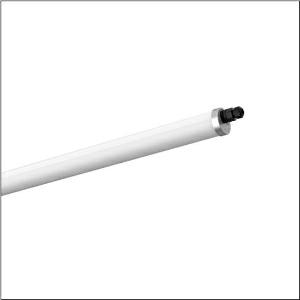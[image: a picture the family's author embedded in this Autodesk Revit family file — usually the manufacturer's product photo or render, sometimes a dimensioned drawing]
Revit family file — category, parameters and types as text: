
# Revit family: monsun_r__31_tube_51ft10dn460a_a449
name_source: partatom
category: Lighting Fixtures
units: mm (PartAtom-declared; Revit-internal decimal feet)

## family parameters
Cut with Voids When Loaded = No
Host = Face
Light Source = No
Part Type = Normal
Room Calculation Point = No
Round Connector Dimension = Use Diameter
Shared = No

## types (1)
- Monsun® 31 Tube (1 x LED, 6500 lm, 40 W, 4000K)
    Apparent Load = 40 VA
    CIE Flux Codes = 42 71 90 91 100
    Color Rendering = 80
    Color Temperature = 4000K
    Default Elevation = 1800 mm
    Description = Monsun® 31 Tube, tubular luminaire, primary optical cover: diffuser, of PMMA, light emission: direct distribution, primary light characteristic: symmetric, installation type: suspended mounting, surface-mounted, LED, rated luminous flux: 6.500lm, luminous efficacy: 160lm/W, light colour: 840, colour temperature: 4000K, with with 1 terminal, 5-pole, max. 2.5mm², through-wiring: 5x 1.5mm², mains connection: 220..240V, AC, 50/60Hz, rated input power: 40W, housing, cylindrical, of PMMA, semi-transparent, matt white, with luminaire and ceiling fastening, V4A, mounting with brackets of stainless steel, length: 1.570mm, diameter: 75mm, end cap, of stainless steel (V4A), protection rating (complete): IP67/IP69K, insulation class (complete): insulation class I (protective earthing), certification: CE, UKCA, impact resistance: IK07, permissible operating ambient temperature: -20..+40°C, corresponds to IFS (International Featured Standards) requirements for safety and quality in the food industry, usage in unprotected outdoor area possible with horizontal mounting, contact your sales advisor before using the luminaires in applications with unclear chemical exposure, large temperature fluctuations or condensation-forming humidity, packaging unit: 1 piece
    Height = 83 mm
    Lamp = 1 x LED
    Lamp Light Flux = 6500 lm
    Lamp Power = 40 W
    Lamp count = 1
    Length = 1570 mm
    Luminous efficacy = 163 lm/W
    Manufacturer = Siteco
    ModVariant = No
    Model = 51FT10DN460A
    Mounting Place = Ceiling
    Mounting Type = Pendant
    Number of Poles = 1
    OnlyDefault = Yes
    Power Factor = 1
    Product Name = Monsun® 31 Tube
    Product group = tubular luminaire
    ProductGroupID = 906
    Protection Class = Protection class I
    RLX_Detail_Level = 1
    RLX_Emergency_Light_Flux = 0 lm
    RLX_Emergency_Type = 0
    RLX_Emergency_Type_DB = No
    RlxData = <blob elided: 25225 chars, md5=b8bb08ee>
    Socket = socket
    Standby Power = 0 W
    System Light Flux = 6500 lm
    System Power = 40 W
    Type Comments = Product without accessories
    Type Image = l_1228461.jpg
    URL = http://relux.com
    VarID = ---
    Voltage = 0 V
    Weight = 0.00 kg
    Width = 75 mm

## geometry (parser evidence)
native form markers: Blend x4, Sweep x12
no freeform markers — native parametric forms only
